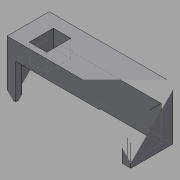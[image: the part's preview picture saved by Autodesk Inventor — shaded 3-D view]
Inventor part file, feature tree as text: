
AUTODESK INVENTOR PART (.ipt)
format: ipt  version: 2015 (Build 190159000, 159)  size: 120,832 bytes
history: native  units: mm
features: extrude x4, sketch x2, plane x1
ambient origin geometry x8: Origin, YZ Plane, XZ Plane, XY Plane, X Axis, Y Axis, Z Axis, Center Point
bodies: Solid1 (feature_tree)
feature tree (7):
  extrude  "Extrusion1"  Depth=6.0mm
  plane  "Work Plane10"
  extrude  "Extrusion25"  Depth=1.0mm TaperAngle=0.0deg
  extrude  "Extrusion26"  Depth=1.0mm TaperAngle=0.0deg
  extrude  "Extrusion27"  Depth=6.0mm TaperAngle=0.0deg
  sketch  "Sketch20"  dims[d1=12.0mm d2=0.0mm d4=6.0mm]
  sketch  "Sketch21"  dims[d108=5.3mm d110=1.0mm d111=0.0mm d112=1.0mm d113=0.0mm d114=6.0mm d115=0.0mm]
